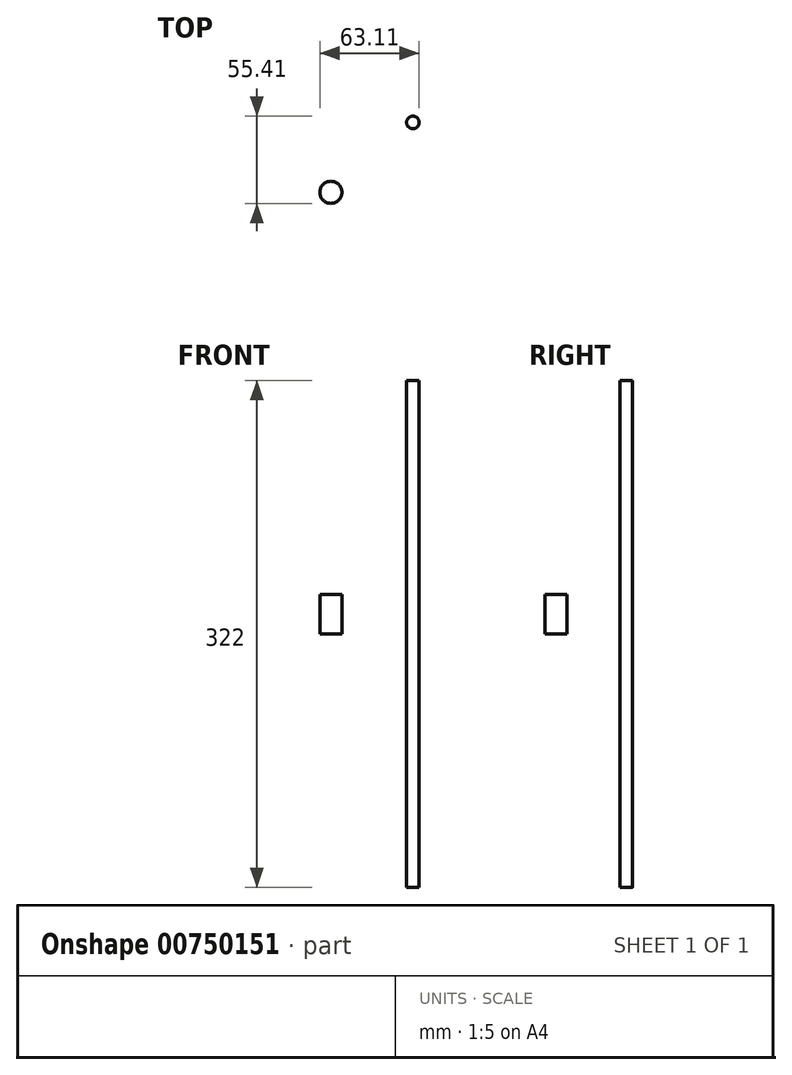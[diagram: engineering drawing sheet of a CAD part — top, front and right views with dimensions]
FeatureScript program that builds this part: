
annotation { "Feature Type Name" : "Feature", "Feature Type Description" : "" }
export const myFeature = defineFeature(function(context is Context, id is Id, definition is map)
    precondition{}
    {
        {
            var Q0;
            Q0=qCreatedBy(makeId("Top.planeOp"),FACE);
            var sketch = newSketch(context, id + "F0", { "sketchPlane" : qUnion([Q0])});
            skCircle(sketch, "E0", {"center": v(0, 0) * mm, "radius": 4 * mm});
            skSolve(sketch);
        }
        {
            var Q0;
            Q0=makeQuery(id+"F0.imprint","IMPRINT",FACE,{"disambiguationData":[TD([[makeQuery(id+"F0.imprint","IMPRINT",EDGE,{"derivedFrom":sQuery(id+"F0.wireOp",EDGE,"E0")}),1.0]])]});
            extrude(context, id + "F1", {"entities" : qUnion([Q0]), "depth" : (220 + 102) * mm, "offsetDistance" : 25 * mm, "symmetric" : true});
        }
        {
            var Q0;
            Q0=qCreatedBy(makeId("Top.planeOp"),FACE);
            var sketch = newSketch(context, id + "F2", { "sketchPlane" : qUnion([Q0])});
            skCircle(sketch, "E1", {"center": v(-52.11, -44.41) * mm, "radius": 7 * mm});
            skSolve(sketch);
        }
        {
            var Q0;
            Q0=makeQuery(id+"F2.imprint","IMPRINT",FACE,{"disambiguationData":[TD([[makeQuery(id+"F2.imprint","IMPRINT",EDGE,{"derivedFrom":sQuery(id+"F2.wireOp",EDGE,"E1")}),1.0]])]});
            extrude(context, id + "F3", {"entities" : qUnion([Q0]), "depth" : 25 * mm, "offsetDistance" : 25 * mm});
        }
    });
